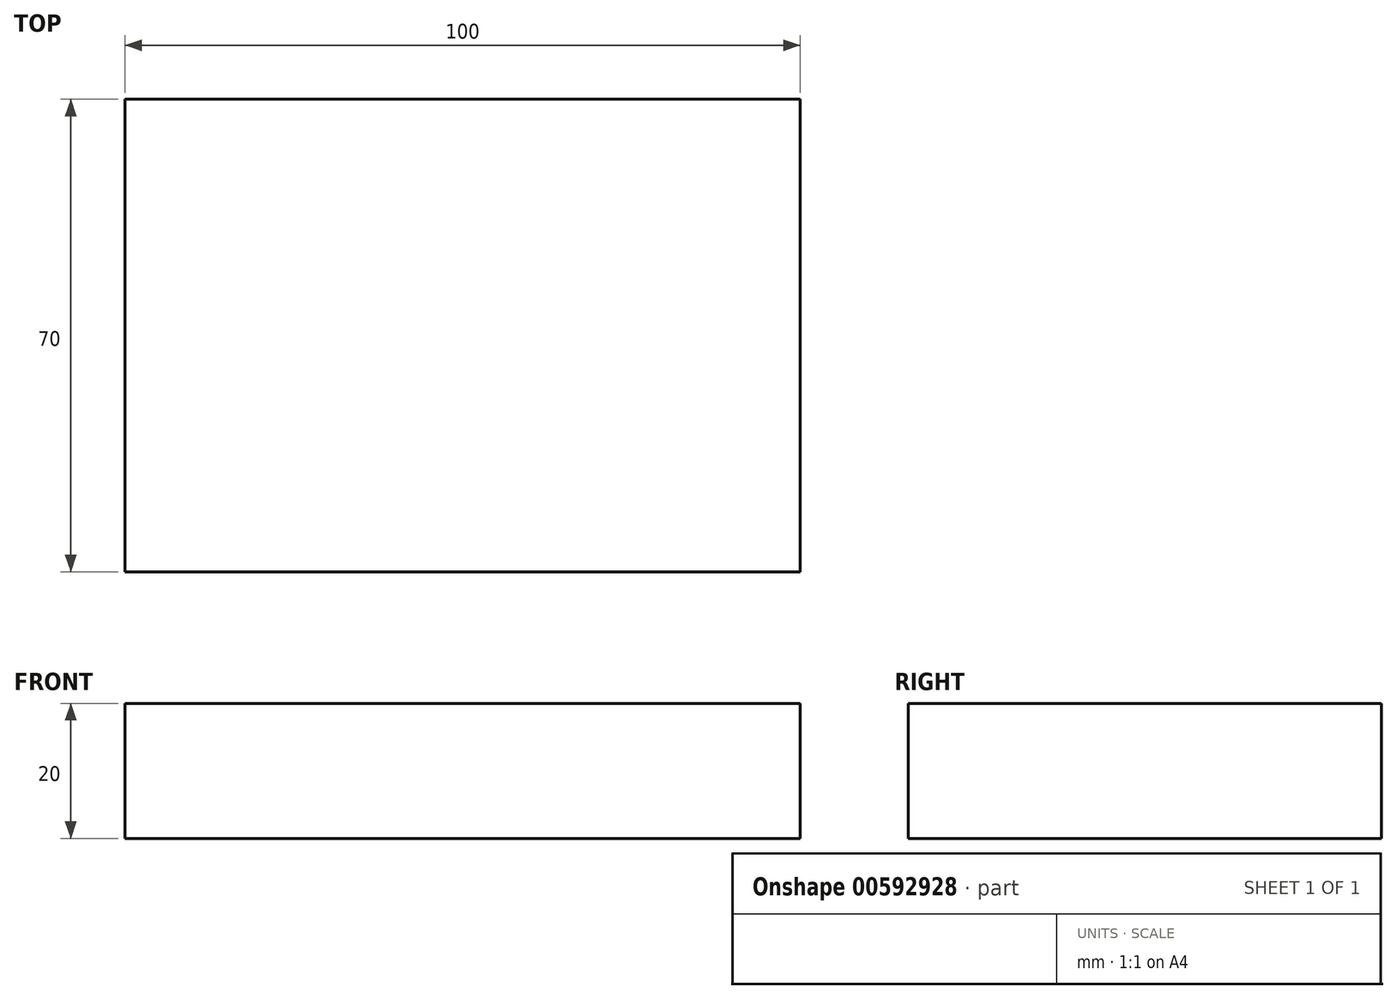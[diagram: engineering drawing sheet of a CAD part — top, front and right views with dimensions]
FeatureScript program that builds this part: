
annotation { "Feature Type Name" : "Feature", "Feature Type Description" : "" }
export const myFeature = defineFeature(function(context is Context, id is Id, definition is map)
    precondition{}
    {
        {
            var Q0;
            Q0=qCreatedBy(makeId("Top.planeOp"),FACE);
            var sketch = newSketch(context, id + "F0", { "sketchPlane" : qUnion([Q0])});
            skLineSegment(sketch, "E0.bottom", {"start": v(0, 0) * mm, "end": v(100, 0) * mm});
            skLineSegment(sketch, "E0.top", {"start": v(0, -70) * mm, "end": v(100, -70) * mm});
            skLineSegment(sketch, "E0.left", {"start": v(0, 0) * mm, "end": v(0, -70) * mm});
            skLineSegment(sketch, "E0.right", {"start": v(100, 0) * mm, "end": v(100, -70) * mm});
            skSolve(sketch);
        }
        {
            var Q0;
            Q0=makeQuery(id+"F0.imprint","IMPRINT",FACE,{"disambiguationData":[TD([[makeQuery(id+"F0.imprint","IMPRINT",EDGE,{"derivedFrom":sQuery(id+"F0.wireOp",EDGE,"E0.bottom")}),-1.0]])]});
            extrude(context, id + "F1", {"entities" : qUnion([Q0]), "depth" : 20 * mm, "offsetDistance" : 25 * mm});
        }
    });
